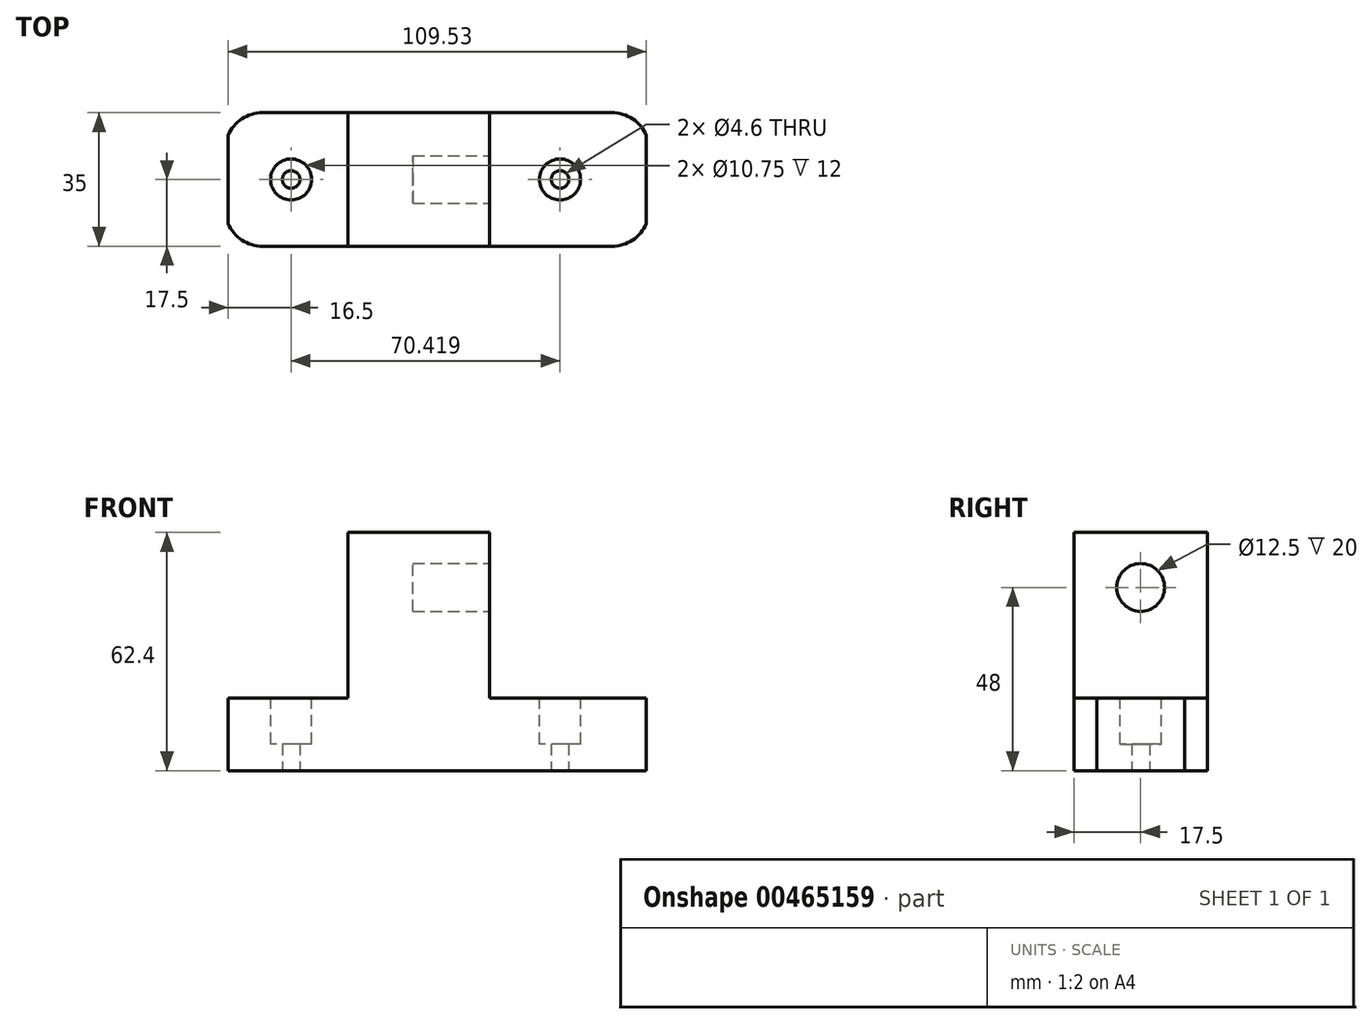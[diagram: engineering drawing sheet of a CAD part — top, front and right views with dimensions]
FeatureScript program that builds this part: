
annotation { "Feature Type Name" : "Feature", "Feature Type Description" : "" }
export const myFeature = defineFeature(function(context is Context, id is Id, definition is map)
    precondition{}
    {
        {
            var Q0;
            Q0=qCreatedBy(makeId("Top.planeOp"),FACE);
            var sketch = newSketch(context, id + "F0", { "sketchPlane" : qUnion([Q0])});
            skCircle(sketch, "E0", {"center": v(0, 0) * mm, "radius": 2.3 * mm});
            skLineSegment(sketch, "E1", {"start": v(0, 0) * mm, "end": v(-16.5, 0) * mm, "construction": true});
            skLineSegment(sketch, "E2", {"start": v(0.12, 0) * mm, "end": v(70.42, 0) * mm, "construction": true});
            skCircle(sketch, "E3", {"center": v(70.42, 0) * mm, "radius": 2.3 * mm});
            skLineSegment(sketch, "E4", {"start": v(-16.5, 0) * mm, "end": v(93.03, 0) * mm, "construction": true});
            skLineSegment(sketch, "E5", {"start": v(38.27, 0) * mm, "end": v(38.27, 17.5) * mm, "construction": true});
            skLineSegment(sketch, "E6", {"start": v(38.27, 0) * mm, "end": v(38.27, -17.5) * mm, "construction": true});
            skLineSegment(sketch, "E7", {"start": v(-16.5, 17.5) * mm, "end": v(-7.5, 17.5) * mm, "construction": true});
            skLineSegment(sketch, "E8", {"start": v(-16.5, -17.5) * mm, "end": v(-7.5, -17.5) * mm, "construction": true});
            skLineSegment(sketch, "E9", {"start": v(93.03, -17.5) * mm, "end": v(84.03, -17.5) * mm, "construction": true});
            skLineSegment(sketch, "E10", {"start": v(93.03, 17.5) * mm, "end": v(84.03, 17.5) * mm, "construction": true});
            skLineSegment(sketch, "E11", {"start": v(-7.5, 17.5) * mm, "end": v(84.03, 17.5) * mm});
            skLineSegment(sketch, "E12", {"start": v(-7.5, -17.5) * mm, "end": v(84.03, -17.5) * mm});
            skLineSegment(sketch, "E13", {"start": v(93.03, 17.5) * mm, "end": v(93.03, 11.5) * mm, "construction": true});
            skLineSegment(sketch, "E14.MirrorCS", {"start": v(93.03, -17.5) * mm, "end": v(93.03, -11.5) * mm, "construction": true});
            skLineSegment(sketch, "E15.MirrorCS", {"start": v(-16.5, 17.5) * mm, "end": v(-16.5, 11.5) * mm, "construction": true});
            skLineSegment(sketch, "E16.MirrorCS", {"start": v(-16.5, -17.5) * mm, "end": v(-16.5, -11.5) * mm, "construction": true});
            skArc(sketch, "E17", {"start": v(93.03, 11.5) * mm, "mid": v(89.44, 15.86) * mm, "end": v(84.03, 17.5) * mm});
            skLineSegment(sketch, "E18", {"start": v(93.03, 11.5) * mm, "end": v(93.03, -11.5) * mm});
            skArc(sketch, "E19.MirrorCS", {"start": v(-16.5, 11.5) * mm, "mid": v(-12.9, 15.86) * mm, "end": v(-7.5, 17.5) * mm});
            skLineSegment(sketch, "E20.MirrorCS", {"start": v(-16.5, 11.5) * mm, "end": v(-16.5, -11.5) * mm});
            skArc(sketch, "E21.MirrorCS", {"start": v(93.03, -11.5) * mm, "mid": v(89.44, -15.86) * mm, "end": v(84.03, -17.5) * mm});
            skArc(sketch, "E22.MirrorCS", {"start": v(-16.5, -11.5) * mm, "mid": v(-12.9, -15.86) * mm, "end": v(-7.5, -17.5) * mm});
            skSolve(sketch);
        }
        {
            var Q0;
            Q0=makeQuery(id+"F0.imprint","IMPRINT",FACE,{"disambiguationData":[TD([[makeQuery(id+"F0.imprint","IMPRINT",EDGE,{"derivedFrom":sQuery(id+"F0.wireOp",EDGE,"E0")}),-1.0]])]});
            extrude(context, id + "F1", {"entities" : qUnion([Q0]), "depth" : 19 * mm});
        }
        {
            var Q0;
            Q0=makeQuery(id+"F1.opExtrude","CAP_FACE",FACE,{"disambiguationData":[OSD([sQuery(id+"F0.wireOp",EDGE,"E0"),sQuery(id+"F0.wireOp",EDGE,"E3"),sQuery(id+"F0.wireOp",EDGE,"E11"),sQuery(id+"F0.wireOp",EDGE,"E12"),sQuery(id+"F0.wireOp",EDGE,"E17"),sQuery(id+"F0.wireOp",EDGE,"E18"),sQuery(id+"F0.wireOp",EDGE,"E19.MirrorCS"),sQuery(id+"F0.wireOp",EDGE,"E20.MirrorCS"),sQuery(id+"F0.wireOp",EDGE,"E21.MirrorCS"),sQuery(id+"F0.wireOp",EDGE,"E22.MirrorCS")])],"isStart":false});
            var sketch = newSketch(context, id + "F2", { "sketchPlane" : qUnion([Q0])});
            skLineSegment(sketch, "E23", {"start": v(-16.5, 0) * mm, "end": v(51.9, 0) * mm, "construction": true});
            skPoint(sketch, "E23.endSnap0", {"position": v(-16.5, 0) * mm});
            skLineSegment(sketch, "E24", {"start": v(51.9, 0) * mm, "end": v(14.9, 0) * mm, "construction": true});
            skLineSegment(sketch, "E25", {"start": v(14.9, 0) * mm, "end": v(14.9, 17.5) * mm});
            skLineSegment(sketch, "E26", {"start": v(14.9, 0) * mm, "end": v(14.9, -17.5) * mm});
            skLineSegment(sketch, "E27", {"start": v(51.9, 0) * mm, "end": v(51.9, -17.5) * mm});
            skLineSegment(sketch, "E28", {"start": v(51.9, 0) * mm, "end": v(51.9, 17.5) * mm});
            skLineSegment(sketch, "E29", {"start": v(51.9, 17.5) * mm, "end": v(14.9, 17.5) * mm});
            skLineSegment(sketch, "E30", {"start": v(14.9, -17.5) * mm, "end": v(51.9, -17.5) * mm});
            skSolve(sketch);
        }
        {
            var Q0;
            Q0=makeQuery(id+"F2.imprint","IMPRINT",FACE,{"disambiguationData":[TD([[makeQuery(id+"F2.imprint","IMPRINT",EDGE,{"derivedFrom":sQuery(id+"F2.wireOp",EDGE,"E25")}),-1.0]])]});
            extrude(context, id + "F3", {"entities" : qUnion([Q0]), "operationType" : NewBodyOperationType.ADD, "depth" : (62.4 - 19) * mm});
        }
        {
            var Q0;
            Q0=qCreatedBy(makeId("Front.planeOp"),FACE);
            var sketch = newSketch(context, id + "F4", { "sketchPlane" : qUnion([Q0])});
            skLineSegment(sketch, "E31.0.0", {"start": v(-7.5, 0) * mm, "end": v(84.03, 0) * mm, "construction": true});
            skLineSegment(sketch, "E31.0.1", {"start": v(84.03, 0) * mm, "end": v(84.03, 19) * mm, "construction": true});
            skLineSegment(sketch, "E31.0.2", {"start": v(84.03, 19) * mm, "end": v(51.9, 19) * mm, "construction": true});
            skLineSegment(sketch, "E31.0.7", {"start": v(-7.5, 19) * mm, "end": v(-7.5, 0) * mm, "construction": true});
            skLineSegment(sketch, "E32", {"start": v(51.9, 19) * mm, "end": v(51.9, 0) * mm, "construction": true});
            skLineSegment(sketch, "E33", {"start": v(51.9, 0) * mm, "end": v(51.9, 48) * mm, "construction": true});
            skSolve(sketch);
        }
        {
            var Q0;
            Q0=makeQuery(id+"F3.opExtrude","SWEPT_FACE",FACE,{"disambiguationData":[OSD([sQuery(id+"F2.wireOp",EDGE,"E27"),sQuery(id+"F2.wireOp",EDGE,"E28")])]});
            var sketch = newSketch(context, id + "F5", { "sketchPlane" : qUnion([Q0])});
            skPoint(sketch, "E34.0", {"position": v(0, 48) * mm});
            skCircle(sketch, "E35", {"center": v(0, 48) * mm, "radius": 6.25 * mm});
            skSolve(sketch);
        }
        {
            var Q0;
            Q0=makeQuery(id+"F5.imprint","IMPRINT",FACE,{"disambiguationData":[TD([[makeQuery(id+"F5.imprint","IMPRINT",EDGE,{"derivedFrom":sQuery(id+"F5.wireOp",EDGE,"E35")}),1.0]])]});
            extrude(context, id + "F6", {"entities" : qUnion([Q0]), "operationType" : NewBodyOperationType.REMOVE, "oppositeDirection" : true, "depth" : 20 * mm});
        }
        {
            var Q0;
            {var subQ0=sQuery(id+"F0.wireOp",EDGE,"E19.MirrorCS");var subQ1=sQuery(id+"F0.wireOp",EDGE,"E11");var subQ2=sQuery(id+"F0.wireOp",EDGE,"E12");var subQ3=sQuery(id+"F0.wireOp",EDGE,"E0");var subQ4=sQuery(id+"F0.wireOp",EDGE,"E22.MirrorCS");var subQ5=sQuery(id+"F0.wireOp",EDGE,"E20.MirrorCS");Q0=makeQuery(id+"F3.boolean.opBoolean","SPLIT",FACE,{"disambiguationData":[TD([makeQuery(id+"F1.opExtrude","SWEPT_FACE",FACE,{"disambiguationData":[OSD([subQ3])]})])],"derivedFrom":makeQuery(id+"F1.opExtrude","CAP_FACE",FACE,{"disambiguationData":[OSD([subQ3,sQuery(id+"F0.wireOp",EDGE,"E3"),subQ1,subQ2,sQuery(id+"F0.wireOp",EDGE,"E17"),sQuery(id+"F0.wireOp",EDGE,"E18"),subQ0,subQ5,sQuery(id+"F0.wireOp",EDGE,"E21.MirrorCS"),subQ4])],"isStart":false})});}
            var sketch = newSketch(context, id + "F7", { "sketchPlane" : qUnion([Q0])});
            skCircle(sketch, "E36", {"center": v(0, 0) * mm, "radius": 5.38 * mm});
            skCircle(sketch, "E37.0", {"center": v(70.42, 0) * mm, "radius": 2.3 * mm, "construction": true});
            skCircle(sketch, "E38", {"center": v(70.42, 0) * mm, "radius": 5.38 * mm});
            skSolve(sketch);
        }
        {
            var Q0;
            Q0=makeQuery(id+"F7.imprint","IMPRINT",FACE,{"disambiguationData":[TD([[makeQuery(id+"F7.imprint","IMPRINT",EDGE,{"derivedFrom":sQuery(id+"F7.wireOp",EDGE,"E36")}),1.0]])]});
            var Q1;
            Q1=makeQuery(id+"F7.imprint","IMPRINT",FACE,{"disambiguationData":[TD([[makeQuery(id+"F7.imprint","IMPRINT",EDGE,{"derivedFrom":sQuery(id+"F7.wireOp",EDGE,"E38")}),1.0]])]});
            extrude(context, id + "F8", {"entities" : qUnion([Q0, Q1]), "operationType" : NewBodyOperationType.REMOVE, "oppositeDirection" : true, "depth" : 12 * mm});
        }
    });
